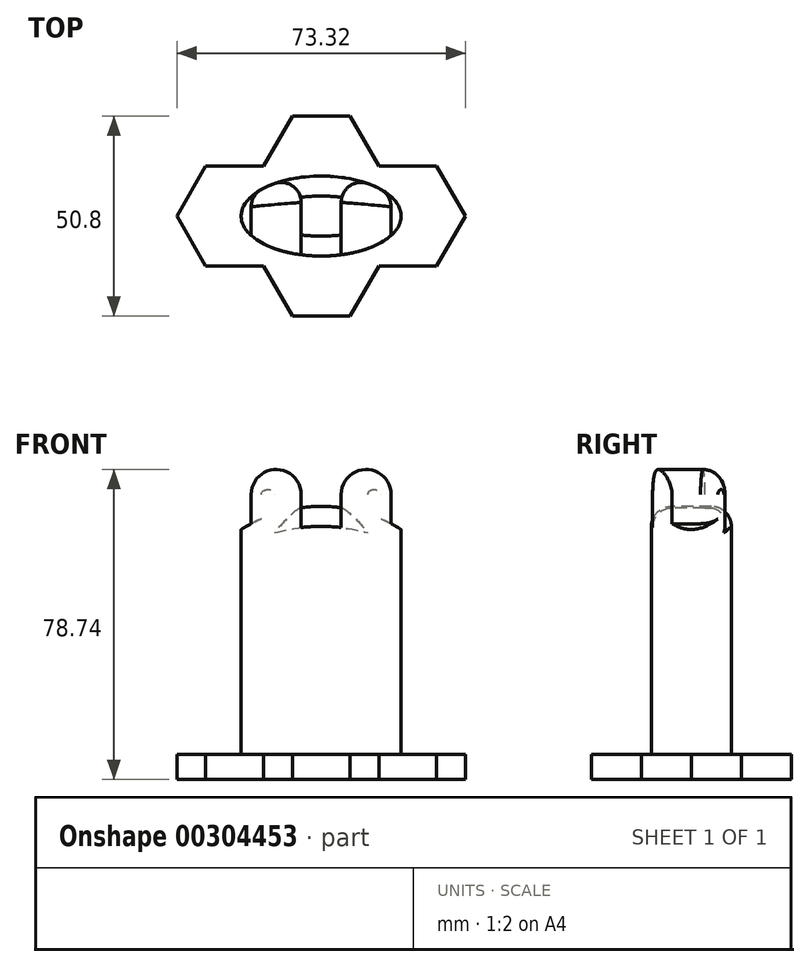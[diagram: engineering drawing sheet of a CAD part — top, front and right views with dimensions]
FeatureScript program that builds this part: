
annotation { "Feature Type Name" : "Feature", "Feature Type Description" : "" }
export const myFeature = defineFeature(function(context is Context, id is Id, definition is map)
    precondition{}
    {
        {
            var Q0;
            Q0=qCreatedBy(makeId("Top.planeOp"),FACE);
            var sketch = newSketch(context, id + "F0", { "sketchPlane" : qUnion([Q0])});
            skCircle(sketch, "E0.cCircle", {"center": v(0, 12.7) * mm, "radius": 12.7 * mm, "construction": true});
            skLineSegment(sketch, "E0.2", {"start": v(-14.66, 12.7) * mm, "end": v(-7.33, 25.4) * mm});
            skLineSegment(sketch, "E0.3", {"start": v(-7.33, 25.4) * mm, "end": v(7.33, 25.4) * mm});
            skLineSegment(sketch, "E0.4", {"start": v(7.33, 25.4) * mm, "end": v(14.66, 12.7) * mm});
            skPoint(sketch, "E0.0.midPoint", {"position": v(0, 0) * mm});
            skLineSegment(sketch, "E1.MirrorCS", {"start": v(-14.66, 12.7) * mm, "end": v(-29.33, 12.7) * mm});
            skLineSegment(sketch, "E2.MirrorCS", {"start": v(-29.33, 12.7) * mm, "end": v(-36.66, 0) * mm});
            skLineSegment(sketch, "E3.MirrorCS", {"start": v(-36.66, 0) * mm, "end": v(-29.33, -12.7) * mm});
            skLineSegment(sketch, "E4.MirrorCS", {"start": v(-29.33, -12.7) * mm, "end": v(-14.66, -12.7) * mm});
            skLineSegment(sketch, "E5.MirrorCS", {"start": v(-7.33, -25.4) * mm, "end": v(-14.66, -12.7) * mm});
            skLineSegment(sketch, "E6.MirrorCS", {"start": v(7.33, -25.4) * mm, "end": v(-7.33, -25.4) * mm});
            skLineSegment(sketch, "E7.MirrorCS", {"start": v(14.66, -12.7) * mm, "end": v(7.33, -25.4) * mm});
            skLineSegment(sketch, "E8.MirrorCS", {"start": v(14.66, -12.7) * mm, "end": v(29.33, -12.7) * mm});
            skLineSegment(sketch, "E9.MirrorCS", {"start": v(29.33, -12.7) * mm, "end": v(36.66, 0) * mm});
            skLineSegment(sketch, "E10.MirrorCS", {"start": v(36.66, 0) * mm, "end": v(29.33, 12.7) * mm});
            skLineSegment(sketch, "E11.MirrorCS", {"start": v(29.33, 12.7) * mm, "end": v(14.66, 12.7) * mm});
            skPoint(sketch, "E12.orphan", {"position": v(-7.33, 0) * mm});
            skPoint(sketch, "E0.5.end.orphan", {"position": v(7.33, 0) * mm});
            skSolve(sketch);
        }
        {
            var Q0;
            Q0 = qSketchRegion(id + "F0", true);
            extrude(context, id + "F1", {"entities" : qUnion([Q0]), "depth" : 6.35 * mm});
        }
        {
            var Q0;
            Q0=makeQuery(id+"F1.opExtrude","CAP_FACE",FACE,{"disambiguationData":[OSD([sQuery(id+"F0.wireOp",EDGE,"E0.2"),sQuery(id+"F0.wireOp",EDGE,"E0.3"),sQuery(id+"F0.wireOp",EDGE,"E0.4"),sQuery(id+"F0.wireOp",EDGE,"E1.MirrorCS"),sQuery(id+"F0.wireOp",EDGE,"E2.MirrorCS"),sQuery(id+"F0.wireOp",EDGE,"E3.MirrorCS"),sQuery(id+"F0.wireOp",EDGE,"E4.MirrorCS"),sQuery(id+"F0.wireOp",EDGE,"E5.MirrorCS"),sQuery(id+"F0.wireOp",EDGE,"E6.MirrorCS"),sQuery(id+"F0.wireOp",EDGE,"E7.MirrorCS"),sQuery(id+"F0.wireOp",EDGE,"E8.MirrorCS"),sQuery(id+"F0.wireOp",EDGE,"E9.MirrorCS"),sQuery(id+"F0.wireOp",EDGE,"E10.MirrorCS"),sQuery(id+"F0.wireOp",EDGE,"E11.MirrorCS")])],"isStart":false});
            var sketch = newSketch(context, id + "F2", { "sketchPlane" : qUnion([Q0])});
            skEllipse(sketch, "E13", {"center": v(0, 0) * mm, "majorRadius": 20.32 * mm, "minorRadius": 10.16 * mm, "majorAxis": v(1, 0)});
            skSolve(sketch);
        }
        {
            var Q0;
            Q0 = qSketchRegion(id + "F2", true);
            extrude(context, id + "F3", {"entities" : qUnion([Q0]), "operationType" : NewBodyOperationType.ADD, "depth" : 76.2 * mm});
        }
        {
            var Q0;
            Q0=qCreatedBy(makeId("Front.planeOp"),FACE);
            var sketch = newSketch(context, id + "F4", { "sketchPlane" : qUnion([Q0])});
            skArc(sketch, "E14", {"start": v(20.32, 63.5) * mm, "mid": v(19.06, 64.26) * mm, "end": v(17.78, 64.97) * mm});
            skLineSegment(sketch, "E15", {"start": v(-20.32, 63.5) * mm, "end": v(-20.32, 88.9) * mm});
            skLineSegment(sketch, "E16", {"start": v(-20.32, 88.9) * mm, "end": v(20.36, 88.9) * mm});
            skLineSegment(sketch, "E17", {"start": v(20.36, 88.9) * mm, "end": v(20.32, 63.5) * mm});
            skArc(sketch, "E18", {"start": v(-5.08, 72.4) * mm, "mid": v(-11.43, 78.74) * mm, "end": v(-17.78, 72.4) * mm});
            skArc(sketch, "E19", {"start": v(17.78, 72.4) * mm, "mid": v(11.43, 78.74) * mm, "end": v(5.08, 72.4) * mm});
            skLineSegment(sketch, "E20", {"start": v(-17.78, 72.4) * mm, "end": v(-17.78, 64.97) * mm});
            skLineSegment(sketch, "E21", {"start": v(-5.08, 72.4) * mm, "end": v(-5.08, 69.03) * mm});
            skLineSegment(sketch, "E22", {"start": v(5.08, 72.4) * mm, "end": v(5.08, 69.03) * mm});
            skLineSegment(sketch, "E23", {"start": v(17.78, 72.4) * mm, "end": v(17.78, 64.97) * mm});
            skArc(sketch, "E24.trimOffspring", {"start": v(-17.78, 64.97) * mm, "mid": v(-19.06, 64.26) * mm, "end": v(-20.32, 63.5) * mm});
            skArc(sketch, "E25.trimOffspring", {"start": v(5.08, 69.03) * mm, "mid": v(0, 69.37) * mm, "end": v(-5.08, 69.03) * mm});
            skSolve(sketch);
        }
        {
            var Q0;
            Q0 = qSketchRegion(id + "F4", true);
            extrude(context, id + "F5", {"entities" : qUnion([Q0]), "operationType" : NewBodyOperationType.REMOVE, "oppositeDirection" : true, "depth" : 25.4 * mm, "hasSecondDirection" : true, "secondDirectionOppositeDirection" : false, "secondDirectionDepth" : 25.4 * mm});
        }
        {
            var Q0;
            Q0=makeQuery(id+"F5.boolean.opBoolean","INTERSECT",EDGE,{"disambiguationData":[OD(1.0)],"derivedFrom":[makeQuery(id+"F3.opExtrude","SWEPT_FACE",FACE,{"disambiguationData":[OSD([sQuery(id+"F2.wireOp",EDGE,"E13")])]}),makeQuery(id+"F5.opExtrude","SWEPT_FACE",FACE,{"disambiguationData":[OSD([sQuery(id+"F4.wireOp",EDGE,"E21")])]})]});
            var Q1;
            Q1=makeQuery(id+"F5.boolean.opBoolean","INTERSECT",EDGE,{"disambiguationData":[OD(1.0)],"derivedFrom":[makeQuery(id+"F3.opExtrude","SWEPT_FACE",FACE,{"disambiguationData":[OSD([sQuery(id+"F2.wireOp",EDGE,"E13")])]}),makeQuery(id+"F5.opExtrude","SWEPT_FACE",FACE,{"disambiguationData":[OSD([sQuery(id+"F4.wireOp",EDGE,"E22")])]})]});
            var Q2;
            Q2=makeQuery(id+"F5.boolean.opBoolean","INTERSECT",EDGE,{"disambiguationData":[OD(1.0)],"derivedFrom":[makeQuery(id+"F3.opExtrude","SWEPT_FACE",FACE,{"disambiguationData":[OSD([sQuery(id+"F2.wireOp",EDGE,"E13")])]}),makeQuery(id+"F5.opExtrude","SWEPT_FACE",FACE,{"disambiguationData":[OSD([sQuery(id+"F4.wireOp",EDGE,"E25.trimOffspring")])]})]});
            var Q3;
            Q3=makeQuery(id+"F5.boolean.opBoolean","INTERSECT",EDGE,{"disambiguationData":[OD(0.0)],"derivedFrom":[makeQuery(id+"F3.opExtrude","SWEPT_FACE",FACE,{"disambiguationData":[OSD([sQuery(id+"F2.wireOp",EDGE,"E13")])]}),makeQuery(id+"F5.opExtrude","SWEPT_FACE",FACE,{"disambiguationData":[OSD([sQuery(id+"F4.wireOp",EDGE,"E25.trimOffspring")])]})]});
            fillet(context, id + "F6", {"entities" : qUnion([Q0, Q1, Q2, Q3]), "radius" : 5.08 * mm, "tangentPropagation" : true, "allowEdgeOverflow" : false});
        }
    });
